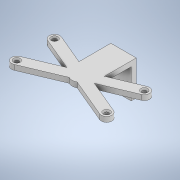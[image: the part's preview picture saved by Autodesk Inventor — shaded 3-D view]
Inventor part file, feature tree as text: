
AUTODESK INVENTOR PART (.ipt)
format: ipt  version: 2021 (Build 250183000, 183)  size: 211,456 bytes
history: native  units: mm
features: extrude x4, sketch x2, other x1, plane x1, chamfer x1
ambient origin geometry x8: Origin, YZ Plane, XZ Plane, XY Plane, X Axis, Y Axis, Z Axis, Center Point
bodies: Body1 (feature_tree)
feature tree (9):
  other  "HC-SR04.ipt"
  extrude  "Extrusion1"  Depth=10.0mm
  extrude  "Extrusion2"  Depth=5.0mm
  plane  "Arbeitsebene1"
  extrude  "Extrusion3"  Depth=5.0mm
  extrude  "Extrusion4"  Depth=5.0mm
  chamfer  "Fase1"  Distance=5.0mm
  sketch  "Skizze3"  dims[d0=10.0mm d1=2.0mm]
  sketch  "Skizze4"  dims[d3=8.0mm d5=5.0mm d6=5.0mm d7=5.0mm d8=5.0mm d9=5.0mm d10=5.0mm d11=5.0mm d12=5.0mm d13=3.0mm d14=12.0mm d15=10.0mm d16=2.4mm d17=2.4mm d18=0.0mm d19=14.0mm d20=0.0mm d21=2.4mm d22=0.0mm d23=0.0mm d25=18.439089mm d26=2.19513mm d27=5.446363mm d28=4.2mm d30=5.446363mm d31=12.0mm d32=0.0mm d33=0.6mm d34=2.0mm d35=45.0deg]
